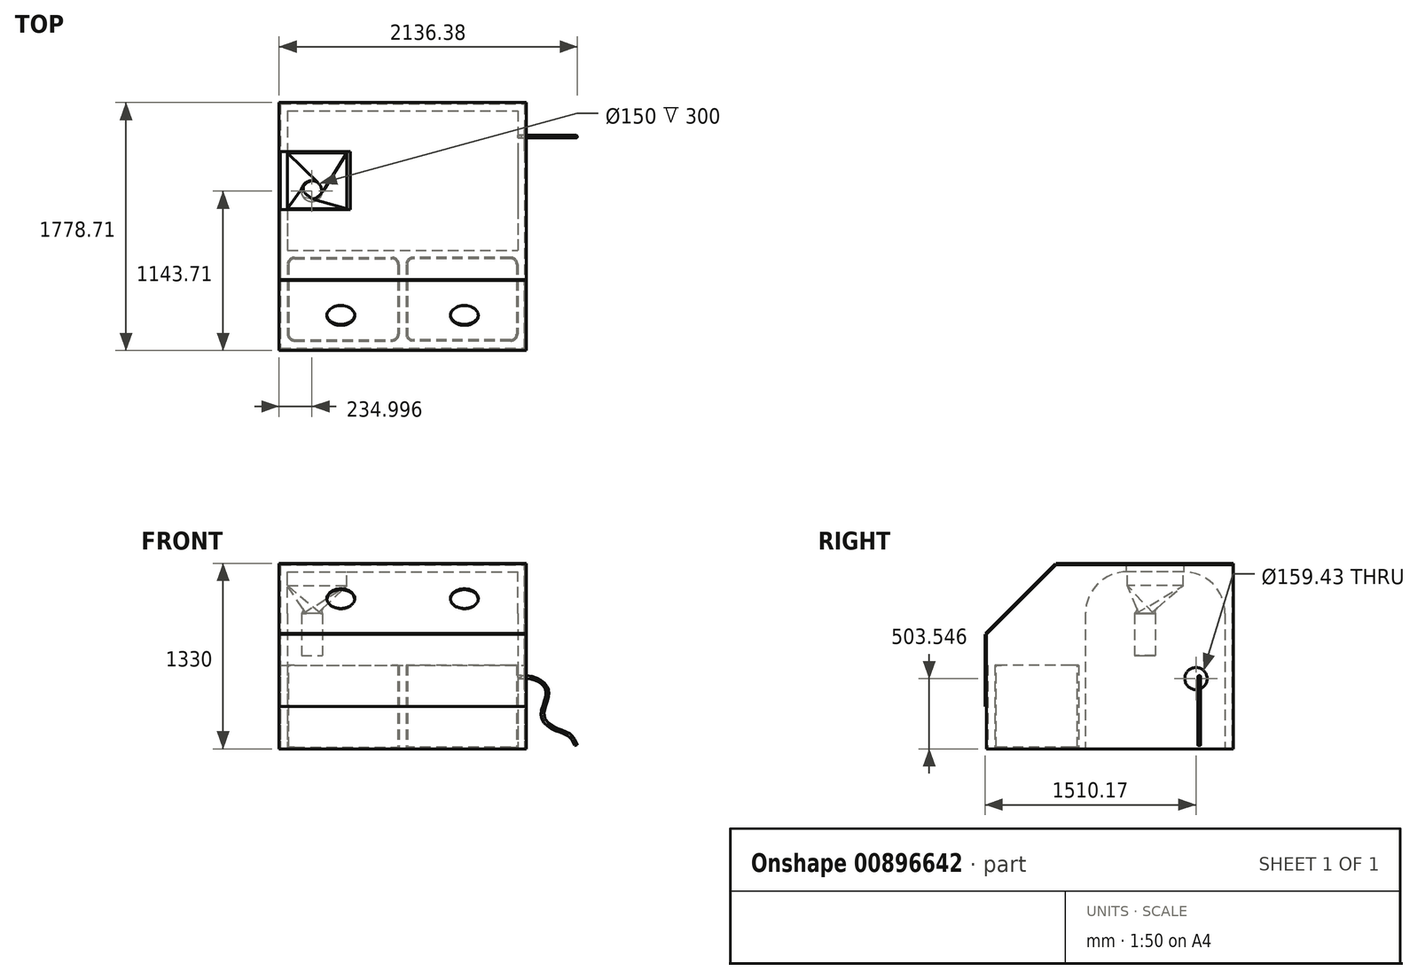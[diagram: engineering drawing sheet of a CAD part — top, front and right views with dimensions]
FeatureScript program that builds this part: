
annotation { "Feature Type Name" : "Feature", "Feature Type Description" : "" }
export const myFeature = defineFeature(function(context is Context, id is Id, definition is map)
    precondition{}
    {
        {
            var Q0;
            Q0=qCreatedBy(makeId("Top.planeOp"),FACE);
            var sketch = newSketch(context, id + "F0", { "sketchPlane" : qUnion([Q0])});
            skLineSegment(sketch, "E0.bottom", {"start": v(-103.43, 936.06) * mm, "end": v(1546.57, 936.06) * mm});
            skLineSegment(sketch, "E0.top", {"start": v(-103.43, -63.94) * mm, "end": v(1546.57, -63.94) * mm});
            skLineSegment(sketch, "E0.left", {"start": v(-103.43, 936.06) * mm, "end": v(-103.43, -63.94) * mm});
            skLineSegment(sketch, "E0.right", {"start": v(1546.57, 936.06) * mm, "end": v(1546.57, -63.94) * mm});
            skSolve(sketch);
        }
        {
            var Q0;
            Q0=makeQuery(id+"F0.imprint","IMPRINT",FACE,{"disambiguationData":[TD([[makeQuery(id+"F0.imprint","IMPRINT",EDGE,{"derivedFrom":sQuery(id+"F0.wireOp",EDGE,"E0.bottom")}),-1.0]])]});
            extrude(context, id + "F1", {"entities" : qUnion([Q0]), "depth" : 1270 * mm, "offsetDistance" : 25.4 * mm});
        }
        {
            var Q0;
            Q0=makeQuery(id+"F1.opExtrude","CAP_EDGE",EDGE,{"disambiguationData":[OSD([sQuery(id+"F0.wireOp",EDGE,"E0.top")])],"isStart":false});
            var Q1;
            Q1=makeQuery(id+"F1.opExtrude","CAP_EDGE",EDGE,{"disambiguationData":[OSD([sQuery(id+"F0.wireOp",EDGE,"E0.bottom")])],"isStart":false});
            fillet(context, id + "F2", {"entities" : qUnion([Q0, Q1]), "radius" : 300 * mm, "tangentPropagation" : true, "allowEdgeOverflow" : false});
        }
        {
            var Q0;
            Q0=makeQuery(id+"F1.opExtrude","CAP_FACE",FACE,{"disambiguationData":[OSD([sQuery(id+"F0.wireOp",EDGE,"E0.bottom"),sQuery(id+"F0.wireOp",EDGE,"E0.top"),sQuery(id+"F0.wireOp",EDGE,"E0.left"),sQuery(id+"F0.wireOp",EDGE,"E0.right")])],"isStart":false});
            var sketch = newSketch(context, id + "F3", { "sketchPlane" : qUnion([Q0])});
            skLineSegment(sketch, "E1.bottom", {"start": v(-103.43, 636.06) * mm, "end": v(323.42, 636.06) * mm});
            skLineSegment(sketch, "E1.top", {"start": v(-103.43, 236.06) * mm, "end": v(323.42, 236.06) * mm});
            skLineSegment(sketch, "E1.left", {"start": v(-103.43, 636.06) * mm, "end": v(-103.43, 236.06) * mm});
            skLineSegment(sketch, "E1.right", {"start": v(323.42, 636.06) * mm, "end": v(323.42, 236.06) * mm});
            skSolve(sketch);
        }
        {
            var Q0;
            Q0 = qSketchRegion(id + "F3", true);
            extrude(context, id + "F4", {"entities" : qUnion([Q0]), "operationType" : NewBodyOperationType.REMOVE, "oppositeDirection" : true, "depth" : 100 * mm, "offsetDistance" : 25.4 * mm});
        }
        {
            var Q0;
            Q0=makeQuery(id+"F1.opExtrude","CAP_FACE",FACE,{"disambiguationData":[OSD([sQuery(id+"F0.wireOp",EDGE,"E0.bottom"),sQuery(id+"F0.wireOp",EDGE,"E0.top"),sQuery(id+"F0.wireOp",EDGE,"E0.left"),sQuery(id+"F0.wireOp",EDGE,"E0.right")])],"isStart":true});
            cPlane(context, id + "F5", {"entities" : qUnion([Q0]), "cplaneType" : CPlaneType.OFFSET, "offset" : 670 * mm, "oppositeDirection" : true, "width" : 152.4 * mm, "height" : 152.4 * mm});
        }
        {
            var Q0;
            Q0=qCreatedBy(id+"F5.planeOp",FACE);
            var sketch = newSketch(context, id + "F6", { "sketchPlane" : qUnion([Q0])});
            skCircle(sketch, "E2", {"center": v(71.57, -361.06) * mm, "radius": 75 * mm});
            skSolve(sketch);
        }
        {
            var Q0;
            Q0 = qSketchRegion(id + "F6", true);
            extrude(context, id + "F7", {"entities" : qUnion([Q0]), "operationType" : NewBodyOperationType.REMOVE, "oppositeDirection" : true, "depth" : 300 * mm, "offsetDistance" : 25.4 * mm});
        }
        {
            var Q0;
            Q0=qCreatedBy(id+"F5.planeOp",FACE);
            cPlane(context, id + "F8", {"entities" : qUnion([Q0]), "cplaneType" : CPlaneType.OFFSET, "offset" : 300 * mm, "oppositeDirection" : true, "width" : 152.4 * mm, "height" : 152.4 * mm});
        }
        {
            var Q0;
            Q0=qCreatedBy(id+"F8.planeOp",FACE);
            var sketch = newSketch(context, id + "F9", { "sketchPlane" : qUnion([Q0])});
            skCircle(sketch, "E3", {"center": v(71.57, -361.06) * mm, "radius": 75 * mm});
            skSolve(sketch);
        }
        {
            var Q1;
            Q1=makeQuery(id+"F9.imprint","IMPRINT",FACE,{"disambiguationData":[TD([[makeQuery(id+"F9.imprint","IMPRINT",EDGE,{"derivedFrom":sQuery(id+"F9.wireOp",EDGE,"E3")}),1.0]])]});
            var Q2;
            Q2=makeQuery(id+"F4.boolean.opBoolean","COPY",FACE,{"derivedFrom":makeQuery(id+"F4.opExtrude","CAP_FACE",FACE,{"disambiguationData":[OSD([sQuery(id+"F3.wireOp",EDGE,"E1.bottom"),sQuery(id+"F3.wireOp",EDGE,"E1.top"),sQuery(id+"F3.wireOp",EDGE,"E1.left"),sQuery(id+"F3.wireOp",EDGE,"E1.right")])],"isStart":false})});
            loft(context, id + "F10", {"operationType" : NewBodyOperationType.REMOVE, "sheetProfilesArray" : [{ "sheetProfileEntities" : qUnion([Q1]) }, { "sheetProfileEntities" : qUnion([Q2]) }]});
        }
        {
            var Q0;
            Q0=qCreatedBy(makeId("Top.planeOp"),FACE);
            var sketch = newSketch(context, id + "F11", { "sketchPlane" : qUnion([Q0])});
            skLineSegment(sketch, "E4.bottom", {"start": v(-53.43, -113.94) * mm, "end": v(646.57, -113.94) * mm});
            skLineSegment(sketch, "E4.top", {"start": v(-53.43, -713.94) * mm, "end": v(646.57, -713.94) * mm});
            skLineSegment(sketch, "E4.left", {"start": v(-103.43, -163.94) * mm, "end": v(-103.43, -663.94) * mm});
            skLineSegment(sketch, "E4.right", {"start": v(696.57, -163.94) * mm, "end": v(696.57, -663.94) * mm});
            skLineSegment(sketch, "E5", {"start": v(696.57, -113.94) * mm, "end": v(721.57, -113.94) * mm, "construction": true});
            skLineSegment(sketch, "E6", {"start": v(721.57, -113.94) * mm, "end": v(721.57, -1034.54) * mm, "construction": true});
            skLineSegment(sketch, "E7.MirrorCS", {"start": v(1496.57, -113.94) * mm, "end": v(796.57, -113.94) * mm});
            skLineSegment(sketch, "E8.MirrorCS", {"start": v(746.57, -163.94) * mm, "end": v(746.57, -663.94) * mm});
            skLineSegment(sketch, "E9.MirrorCS", {"start": v(1496.57, -713.94) * mm, "end": v(796.57, -713.94) * mm});
            skLineSegment(sketch, "E10.MirrorCS", {"start": v(1546.57, -163.94) * mm, "end": v(1546.57, -663.94) * mm});
            skPoint(sketch, "E11.visualSharp", {"position": v(-103.43, -113.94) * mm});
            skArc(sketch, "E11.filletArc", {"start": v(-53.43, -113.94) * mm, "mid": v(-88.79, -128.58) * mm, "end": v(-103.43, -163.94) * mm});
            skPoint(sketch, "E12.visualSharp", {"position": v(696.57, -113.94) * mm});
            skArc(sketch, "E12.filletArc", {"start": v(696.57, -163.94) * mm, "mid": v(681.92, -128.58) * mm, "end": v(646.57, -113.94) * mm});
            skPoint(sketch, "E13.visualSharp", {"position": v(-103.43, -713.94) * mm});
            skArc(sketch, "E13.filletArc", {"start": v(-103.43, -663.94) * mm, "mid": v(-88.79, -699.3) * mm, "end": v(-53.43, -713.94) * mm});
            skPoint(sketch, "E14.visualSharp", {"position": v(696.57, -713.94) * mm});
            skArc(sketch, "E14.filletArc", {"start": v(646.57, -713.94) * mm, "mid": v(681.92, -699.3) * mm, "end": v(696.57, -663.94) * mm});
            skPoint(sketch, "E15.visualSharp", {"position": v(746.57, -713.94) * mm});
            skArc(sketch, "E15.filletArc", {"start": v(746.57, -663.94) * mm, "mid": v(761.21, -699.3) * mm, "end": v(796.57, -713.94) * mm});
            skPoint(sketch, "E16.visualSharp", {"position": v(746.57, -113.94) * mm});
            skArc(sketch, "E16.filletArc", {"start": v(796.57, -113.94) * mm, "mid": v(761.21, -128.58) * mm, "end": v(746.57, -163.94) * mm});
            skPoint(sketch, "E17.visualSharp", {"position": v(1546.57, -113.94) * mm});
            skArc(sketch, "E17.filletArc", {"start": v(1546.57, -163.94) * mm, "mid": v(1531.92, -128.58) * mm, "end": v(1496.57, -113.94) * mm});
            skPoint(sketch, "E18.visualSharp", {"position": v(1546.57, -713.94) * mm});
            skArc(sketch, "E18.filletArc", {"start": v(1496.57, -713.94) * mm, "mid": v(1531.92, -699.3) * mm, "end": v(1546.57, -663.94) * mm});
            skSolve(sketch);
        }
        {
            var Q0;
            Q0 = qSketchRegion(id + "F11", true);
            extrude(context, id + "F12", {"entities" : qUnion([Q0]), "depth" : 600 * mm, "offsetDistance" : 25.4 * mm});
        }
        {
            var Q0;
            Q0=makeQuery(id+"F12.opExtrude","CAP_FACE",FACE,{"disambiguationData":[OSD([sQuery(id+"F11.wireOp",EDGE,"E4.bottom"),sQuery(id+"F11.wireOp",EDGE,"E4.top"),sQuery(id+"F11.wireOp",EDGE,"E4.left"),sQuery(id+"F11.wireOp",EDGE,"E4.right")])],"isStart":false});
            shell(context, id + "F13", {"entities" : qUnion([Q0]), "thickness" : 10 * mm});
        }
        {
            var Q0;
            Q0=makeQuery(id+"F12.opExtrude","CAP_FACE",FACE,{"disambiguationData":[OSD([sQuery(id+"F11.wireOp",EDGE,"E7.MirrorCS"),sQuery(id+"F11.wireOp",EDGE,"E8.MirrorCS"),sQuery(id+"F11.wireOp",EDGE,"E9.MirrorCS"),sQuery(id+"F11.wireOp",EDGE,"E10.MirrorCS")])],"isStart":false});
            shell(context, id + "F14", {"entities" : qUnion([Q0]), "thickness" : 10 * mm});
        }
        {
            var Q0;
            Q0=qCreatedBy(makeId("Top.planeOp"),FACE);
            var sketch = newSketch(context, id + "F15", { "sketchPlane" : qUnion([Q0])});
            skLineSegment(sketch, "E19.bottom", {"start": v(-163.43, 996.06) * mm, "end": v(1606.57, 996.06) * mm});
            skLineSegment(sketch, "E19.top", {"start": v(-163.43, -773.94) * mm, "end": v(1606.57, -773.94) * mm});
            skLineSegment(sketch, "E19.left", {"start": v(-163.43, 996.06) * mm, "end": v(-163.43, -773.94) * mm});
            skLineSegment(sketch, "E19.right", {"start": v(1606.57, 996.06) * mm, "end": v(1606.57, -773.94) * mm});
            skLineSegment(sketch, "E20.bottom", {"start": v(-153.43, 986.06) * mm, "end": v(1596.57, 986.06) * mm});
            skLineSegment(sketch, "E20.top", {"start": v(-153.43, -763.94) * mm, "end": v(1596.57, -763.94) * mm});
            skLineSegment(sketch, "E20.left", {"start": v(-153.43, 986.06) * mm, "end": v(-153.43, -763.94) * mm});
            skLineSegment(sketch, "E20.right", {"start": v(1596.57, 986.06) * mm, "end": v(1596.57, -763.94) * mm});
            skSolve(sketch);
        }
        {
            var Q0;
            Q0 = qSketchRegion(id + "F15", true);
            extrude(context, id + "F16", {"entities" : qUnion([Q0]), "depth" : 1320 * mm, "offsetDistance" : 25.4 * mm});
        }
        {
            var Q0;
            Q0=makeQuery(id+"F16.opExtrude","CAP_FACE",FACE,{"disambiguationData":[OSD([sQuery(id+"F15.wireOp",EDGE,"E19.bottom"),sQuery(id+"F15.wireOp",EDGE,"E19.top"),sQuery(id+"F15.wireOp",EDGE,"E19.left"),sQuery(id+"F15.wireOp",EDGE,"E19.right"),sQuery(id+"F15.wireOp",EDGE,"E20.bottom"),sQuery(id+"F15.wireOp",EDGE,"E20.top"),sQuery(id+"F15.wireOp",EDGE,"E20.left"),sQuery(id+"F15.wireOp",EDGE,"E20.right")])],"isStart":false});
            var sketch = newSketch(context, id + "F17", { "sketchPlane" : qUnion([Q0])});
            skLineSegment(sketch, "E21.bottom", {"start": v(-153.43, -763.94) * mm, "end": v(1596.57, -763.94) * mm});
            skLineSegment(sketch, "E21.top", {"start": v(-153.43, -773.94) * mm, "end": v(1596.57, -773.94) * mm});
            skLineSegment(sketch, "E21.left", {"start": v(-153.43, -763.94) * mm, "end": v(-153.43, -773.94) * mm});
            skLineSegment(sketch, "E21.right", {"start": v(1596.57, -763.94) * mm, "end": v(1596.57, -773.94) * mm});
            skSolve(sketch);
        }
        {
            var Q0;
            Q0 = qSketchRegion(id + "F17", true);
            extrude(context, id + "F18", {"entities" : qUnion([Q0]), "operationType" : NewBodyOperationType.REMOVE, "oppositeDirection" : true, "depth" : 720 * mm, "offsetDistance" : 25.4 * mm});
        }
        {
            var Q0;
            {var subQ0=sQuery(id+"F15.wireOp",EDGE,"E19.left");var subQ2=sQuery(id+"F15.wireOp",EDGE,"E19.top");Q0=makeQuery(id+"F18.boolean.opBoolean","SPLIT",EDGE,{"disambiguationData":[TD([makeQuery(id+"F16.opExtrude","SWEPT_FACE",FACE,{"disambiguationData":[OSD([subQ0])]})])],"derivedFrom":makeQuery(id+"F16.opExtrude","CAP_EDGE",EDGE,{"disambiguationData":[OSD([subQ2])],"isStart":false})});}
            var Q1;
            {var subQ1=sQuery(id+"F15.wireOp",EDGE,"E19.right");var subQ2=sQuery(id+"F15.wireOp",EDGE,"E19.top");Q1=makeQuery(id+"F18.boolean.opBoolean","SPLIT",EDGE,{"disambiguationData":[TD([makeQuery(id+"F16.opExtrude","SWEPT_FACE",FACE,{"disambiguationData":[OSD([subQ1])]})])],"derivedFrom":makeQuery(id+"F16.opExtrude","CAP_EDGE",EDGE,{"disambiguationData":[OSD([subQ2])],"isStart":false})});}
            chamfer(context, id + "F19", {"entities" : qUnion([Q0, Q1]), "width" : 500 * mm, "tangentPropagation" : true});
        }
        {
            var Q0;
            Q0=makeQuery(id+"F16.opExtrude","SWEPT_FACE",FACE,{"disambiguationData":[OSD([sQuery(id+"F15.wireOp",EDGE,"E19.left")])]});
            var sketch = newSketch(context, id + "F20", { "sketchPlane" : qUnion([Q0])});
            skLineSegment(sketch, "E22.bottom", {"start": v(-996.06, 1320) * mm, "end": v(273.94, 1320) * mm});
            skLineSegment(sketch, "E22.top", {"start": v(-996.06, 1330) * mm, "end": v(273.94, 1330) * mm});
            skLineSegment(sketch, "E22.left", {"start": v(-996.06, 1320) * mm, "end": v(-996.06, 1330) * mm});
            skLineSegment(sketch, "E22.right", {"start": v(273.94, 1320) * mm, "end": v(273.94, 1330) * mm});
            skLineSegment(sketch, "E23", {"start": v(274.26, 1319.68) * mm, "end": v(773.94, 820) * mm});
            skLineSegment(sketch, "E24", {"start": v(773.94, 820) * mm, "end": v(781, 827.07) * mm});
            skLineSegment(sketch, "E25", {"start": v(781, 827.07) * mm, "end": v(281, 1327.07) * mm});
            skLineSegment(sketch, "E26", {"start": v(275.06, 1321.12) * mm, "end": v(281, 1327.07) * mm});
            skLineSegment(sketch, "E27", {"start": v(275.06, 1321.12) * mm, "end": v(274.26, 1319.68) * mm});
            skLineSegment(sketch, "E28", {"start": v(777.52, 820) * mm, "end": v(782.65, 820) * mm});
            skLineSegment(sketch, "E29", {"start": v(782.65, 820) * mm, "end": v(782.65, 305) * mm});
            skLineSegment(sketch, "E30", {"start": v(782.65, 305) * mm, "end": v(773.94, 305) * mm});
            skLineSegment(sketch, "E31", {"start": v(773.94, 305) * mm, "end": v(773.94, 816.42) * mm});
            skLineSegment(sketch, "E32", {"start": v(773.94, 816.42) * mm, "end": v(777.52, 820) * mm});
            skSolve(sketch);
        }
        {
            var Q0;
            Q0 = qSketchRegion(id + "F20", true);
            extrude(context, id + "F21", {"entities" : qUnion([Q0]), "oppositeDirection" : true, "depth" : 1770 * mm, "offsetDistance" : 25.4 * mm});
        }
        {
            var Q0;
            Q0=makeQuery(id+"F21.opExtrude","SWEPT_FACE",FACE,{"disambiguationData":[OSD([sQuery(id+"F20.wireOp",EDGE,"E25")])]});
            var sketch = newSketch(context, id + "F22", { "sketchPlane" : qUnion([Q0])});
            skLineSegment(sketch, "E33", {"start": v(-163.43, 739.68) * mm, "end": v(-163.43, 32.57) * mm, "construction": true});
            skLineSegment(sketch, "E34", {"start": v(-163.43, 386.12) * mm, "end": v(721.57, 386.12) * mm, "construction": true});
            skLineSegment(sketch, "E35", {"start": v(721.57, 386.12) * mm, "end": v(721.57, 739.68) * mm, "construction": true});
            skPoint(sketch, "E36.orphan", {"position": v(1606.57, 386.12) * mm});
            skLineSegment(sketch, "E37", {"start": v(721.57, 386.12) * mm, "end": v(1606.57, 386.12) * mm, "construction": true});
            skCircle(sketch, "E38", {"center": v(279.07, 386.12) * mm, "radius": 100 * mm});
            skCircle(sketch, "E39", {"center": v(1164.07, 386.12) * mm, "radius": 100 * mm});
            skSolve(sketch);
        }
        {
            var Q0;
            Q0 = qSketchRegion(id + "F22", true);
            extrude(context, id + "F23", {"entities" : qUnion([Q0]), "operationType" : NewBodyOperationType.REMOVE, "oppositeDirection" : true, "depth" : 10 * mm, "offsetDistance" : 25.4 * mm});
        }
        {
            var Q0;
            Q0=makeQuery(id+"F16.opExtrude","SWEPT_FACE",FACE,{"disambiguationData":[OSD([sQuery(id+"F15.wireOp",EDGE,"E19.right")])]});
            var sketch = newSketch(context, id + "F24", { "sketchPlane" : qUnion([Q0])});
            skCircle(sketch, "E40", {"center": v(727.52, 503.55) * mm, "radius": 79.72 * mm});
            skSolve(sketch);
        }
        {
            var Q0;
            Q0 = qSketchRegion(id + "F24", true);
            extrude(context, id + "F25", {"entities" : qUnion([Q0]), "operationType" : NewBodyOperationType.REMOVE, "oppositeDirection" : true, "depth" : 25.4 * mm, "offsetDistance" : 25.4 * mm});
        }
        {
            var Q0;
            Q0=makeQuery(id+"F21.opExtrude","SWEPT_FACE",FACE,{"disambiguationData":[OSD([sQuery(id+"F20.wireOp",EDGE,"E22.top")])]});
            var sketch = newSketch(context, id + "F26", { "sketchPlane" : qUnion([Q0])});
            skLineSegment(sketch, "E41", {"start": v(-163.43, 644.5) * mm, "end": v(348.42, 644.5) * mm});
            skLineSegment(sketch, "E42", {"start": v(348.42, 644.5) * mm, "end": v(348.42, 228.53) * mm});
            skLineSegment(sketch, "E43", {"start": v(348.42, 228.53) * mm, "end": v(-163.43, 228.53) * mm});
            skLineSegment(sketch, "E44", {"start": v(-163.43, 228.53) * mm, "end": v(-163.43, 644.5) * mm});
            skSolve(sketch);
        }
        {
            var Q0;
            Q0 = qSketchRegion(id + "F26", true);
            extrude(context, id + "F27", {"entities" : qUnion([Q0]), "operationType" : NewBodyOperationType.REMOVE, "oppositeDirection" : true, "depth" : 50 * mm, "offsetDistance" : 25.4 * mm});
        }
        {
            var Q0;
            Q0=makeQuery(id+"F16.opExtrude","CAP_FACE",FACE,{"disambiguationData":[OSD([sQuery(id+"F15.wireOp",EDGE,"E19.bottom"),sQuery(id+"F15.wireOp",EDGE,"E19.top"),sQuery(id+"F15.wireOp",EDGE,"E19.left"),sQuery(id+"F15.wireOp",EDGE,"E19.right"),sQuery(id+"F15.wireOp",EDGE,"E20.bottom"),sQuery(id+"F15.wireOp",EDGE,"E20.top"),sQuery(id+"F15.wireOp",EDGE,"E20.left"),sQuery(id+"F15.wireOp",EDGE,"E20.right")])],"isStart":false});
            var sketch = newSketch(context, id + "F28", { "sketchPlane" : qUnion([Q0])});
            skLineSegment(sketch, "E45", {"start": v(-163.43, 644.52) * mm, "end": v(-153.43, 644.52) * mm});
            skLineSegment(sketch, "E46", {"start": v(-153.43, 644.52) * mm, "end": v(-153.43, 228.54) * mm});
            skLineSegment(sketch, "E47", {"start": v(-153.43, 228.54) * mm, "end": v(-163.43, 228.54) * mm});
            skLineSegment(sketch, "E48", {"start": v(-163.43, 228.54) * mm, "end": v(-163.43, 644.52) * mm});
            skSolve(sketch);
        }
        {
            var Q0;
            Q0 = qSketchRegion(id + "F28", true);
            extrude(context, id + "F29", {"entities" : qUnion([Q0]), "operationType" : NewBodyOperationType.REMOVE, "oppositeDirection" : true, "depth" : 50 * mm, "offsetDistance" : 25.4 * mm});
        }
        {
            var Q0;
            Q0=makeQuery(id+"F16.opExtrude","SWEPT_FACE",FACE,{"disambiguationData":[OSD([sQuery(id+"F15.wireOp",EDGE,"E19.bottom")])]});
            cPlane(context, id + "F30", {"entities" : qUnion([Q0]), "cplaneType" : CPlaneType.OFFSET, "offset" : 245 * mm, "oppositeDirection" : true, "width" : 152.4 * mm, "height" : 152.4 * mm});
        }
        {
            var Q0;
            Q0=qCreatedBy(id+"F30.planeOp",FACE);
            var sketch = newSketch(context, id + "F31", { "sketchPlane" : qUnion([Q0])});
            skFitSpline(sketch, "E49", {"points": [v(-1482.5, 505.28) * mm, v(-1660.7, 505.28) * mm, v(-1758.72, 410.76) * mm, v(-1723.08, 246.94) * mm, v(-1794.37, 152.43) * mm, v(-1919.12, 95.72) * mm, v(-1963.67, 26.41) * mm], "startDerivative": vector(-959.38, 132.92) * mm, "endDerivative": vector(-241.92, -589.86) * mm});
            skSolve(sketch);
        }
        {
            var Q0;
            Q0=makeQuery(id+"F1.opExtrude","SWEPT_FACE",FACE,{"disambiguationData":[OSD([sQuery(id+"F0.wireOp",EDGE,"E0.right")])]});
            var sketch = newSketch(context, id + "F32", { "sketchPlane" : qUnion([Q0])});
            skCircle(sketch, "E50", {"center": v(751.17, 514.64) * mm, "radius": 10 * mm});
            skSolve(sketch);
        }
        {
            var Q0;
            Q0 = qSketchRegion(id + "F32", true);
            extrude(context, id + "F33", {"entities" : qUnion([Q0]), "operationType" : NewBodyOperationType.ADD, "depth" : 25.4 * mm, "offsetDistance" : 25.4 * mm});
        }
        {
            var Q0;
            Q0=makeQuery(id+"F33.opExtrude","CAP_FACE",FACE,{"disambiguationData":[OSD([sQuery(id+"F32.wireOp",EDGE,"E50")])],"isStart":false});
            var Q1;
            Q1=sQuery(id+"F31.wireOp",EDGE,"E49");
            sweep(context, id + "F34", {"operationType" : NewBodyOperationType.ADD, "profiles" : qUnion([Q0]), "path" : qUnion([Q1])});
        }
    });
